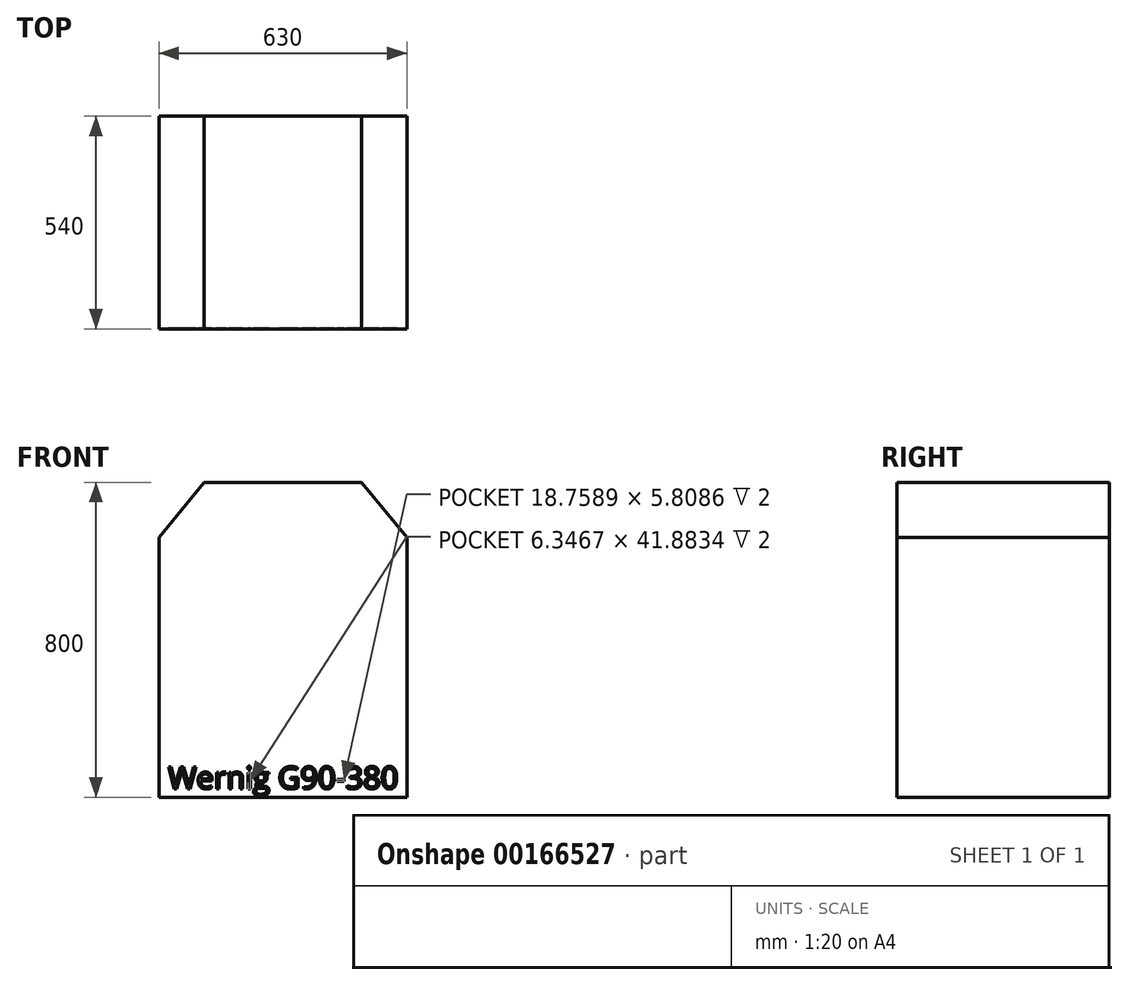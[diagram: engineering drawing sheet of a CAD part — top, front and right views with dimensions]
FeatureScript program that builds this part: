
annotation { "Feature Type Name" : "Feature", "Feature Type Description" : "" }
export const myFeature = defineFeature(function(context is Context, id is Id, definition is map)
    precondition{}
    {
        {
            var Q0;
            Q0=qCreatedBy(makeId("Front.planeOp"),FACE);
            var sketch = newSketch(context, id + "F0", { "sketchPlane" : qUnion([Q0])});
            skLineSegment(sketch, "E0.left", {"start": v(0, 0) * mm, "end": v(0, 660) * mm});
            skLineSegment(sketch, "E1", {"start": v(315, 800) * mm, "end": v(115, 800) * mm});
            skLineSegment(sketch, "E2", {"start": v(115, 800) * mm, "end": v(0, 660) * mm});
            skLineSegment(sketch, "E3", {"start": v(0, 0) * mm, "end": v(315, 0) * mm});
            skLineSegment(sketch, "E4", {"start": v(315, 800) * mm, "end": v(315, 0) * mm, "construction": true});
            skLineSegment(sketch, "E5.MirrorCS", {"start": v(630, 0) * mm, "end": v(315, 0) * mm});
            skLineSegment(sketch, "E6.MirrorCS", {"start": v(630, 0) * mm, "end": v(630, 660) * mm});
            skLineSegment(sketch, "E7.MirrorCS", {"start": v(315, 800) * mm, "end": v(515, 800) * mm});
            skLineSegment(sketch, "E8.MirrorCS", {"start": v(515, 800) * mm, "end": v(630, 660) * mm});
            skSolve(sketch);
        }
        {
            var Q0;
            Q0=makeQuery(id+"F0.imprint","IMPRINT",FACE,{"disambiguationData":[TD([[makeQuery(id+"F0.imprint","IMPRINT",EDGE,{"derivedFrom":sQuery(id+"F0.wireOp",EDGE,"E0.left")}),-1.0]])]});
            extrude(context, id + "F1", {"entities" : qUnion([Q0]), "depth" : 540 * mm});
        }
        {
            var Q0;
            Q0=makeQuery(id+"F1.opExtrude","CAP_FACE",FACE,{"disambiguationData":[OSD([sQuery(id+"F0.wireOp",EDGE,"E0.left"),sQuery(id+"F0.wireOp",EDGE,"E1"),sQuery(id+"F0.wireOp",EDGE,"E2"),sQuery(id+"F0.wireOp",EDGE,"E3"),sQuery(id+"F0.wireOp",EDGE,"E5.MirrorCS"),sQuery(id+"F0.wireOp",EDGE,"E6.MirrorCS"),sQuery(id+"F0.wireOp",EDGE,"E7.MirrorCS"),sQuery(id+"F0.wireOp",EDGE,"E8.MirrorCS")])],"isStart":false});
            var sketch = newSketch(context, id + "F2", { "sketchPlane" : qUnion([Q0])});
            skText(sketch, "E9", { "text": "Wernig G90-380", "fontName": "OpenSans-Regular.ttf"});
            const initialGuessF2  = {"E9": [0.02288, 0.02158, 1, 0, 0.05635]};
            skSetInitialGuess(sketch, initialGuessF2);
            skSolve(sketch);
        }
        {
            var Q0;
            Q0 = qSketchRegion(id + "F2", true);
            extrude(context, id + "F3", {"entities" : qUnion([Q0]), "operationType" : NewBodyOperationType.REMOVE, "oppositeDirection" : true, "depth" : 2 * mm});
        }
    });
